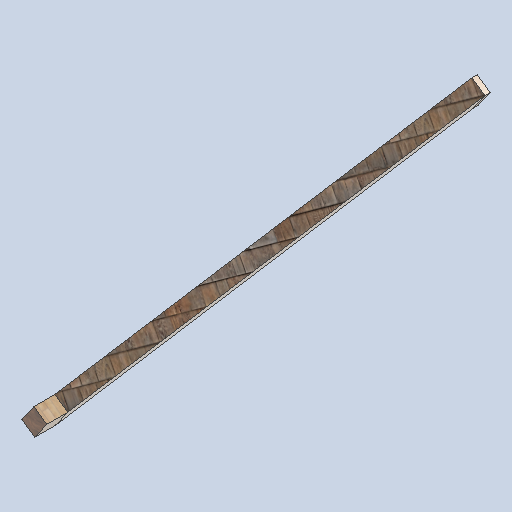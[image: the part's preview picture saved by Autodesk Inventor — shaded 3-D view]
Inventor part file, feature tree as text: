
AUTODESK INVENTOR PART (.ipt)
format: ipt  version: 2024.2 (Build 282272000, 272)  size: 144,384 bytes
history: native  units: in
note: dims shown in document units (in); Inventor stores cm internally (conversion verified against a paired STEP export)
features: sketch x4, other x3, plane x2
ambient origin geometry x8: Origin, YZ Plane, XZ Plane, XY Plane, X Axis, Y Axis, Z Axis, Center Point
bodies: Solid1 (feature_tree)
feature tree (9):
  other  "support_beam_segment_0102.ipt"
  other  "Solid1::support_beam_segment_0102.ipt"
  other  "TaggingFeature1"
  sketch  "Sketch1"  dims[d0=0.3937in]
  sketch  "Sketch2"
  sketch  "Sketch3"
  sketch  "Sketch4"
  plane  "Work Plane1"
  plane  "Work Plane2"
